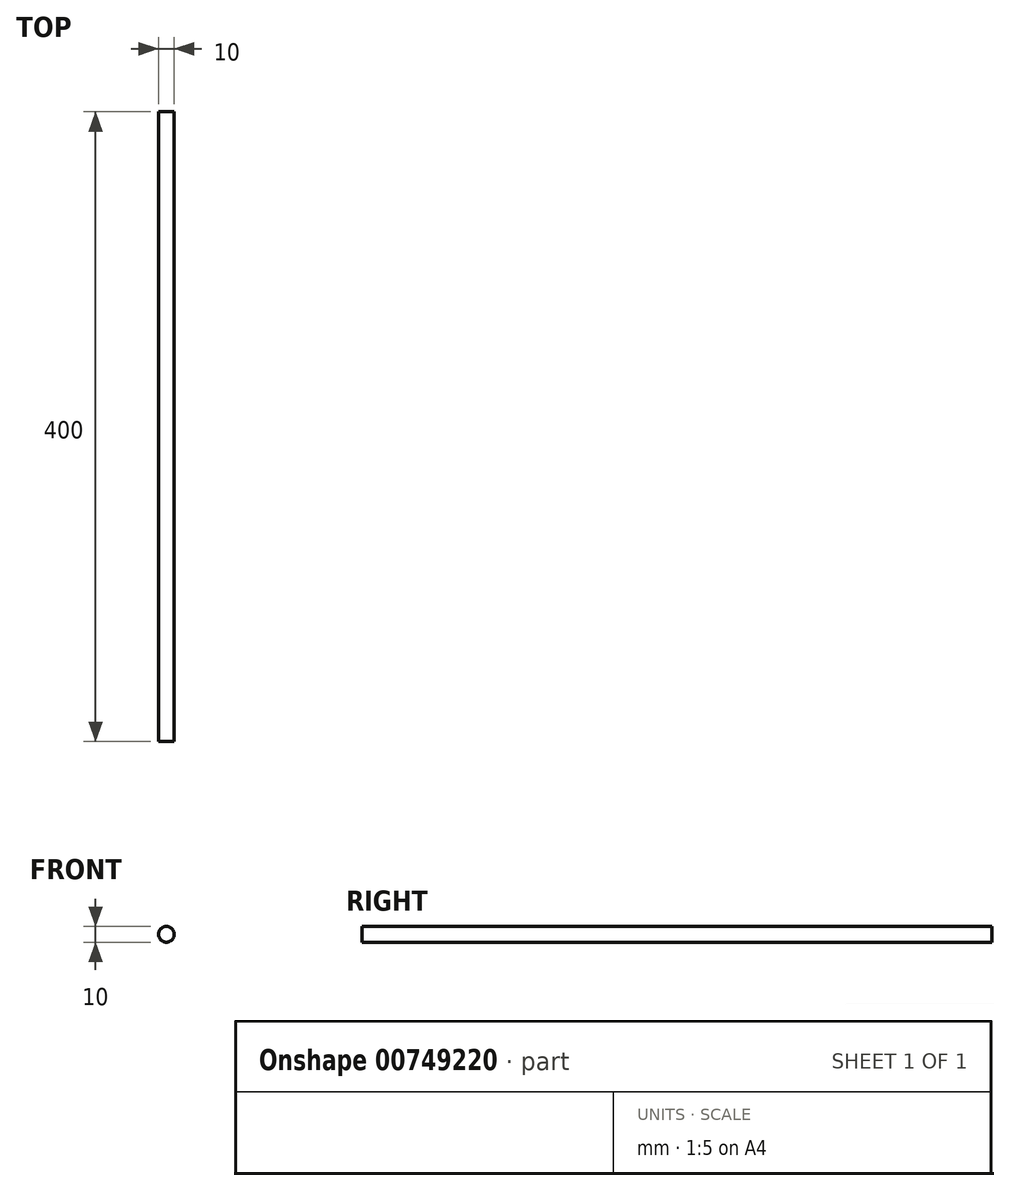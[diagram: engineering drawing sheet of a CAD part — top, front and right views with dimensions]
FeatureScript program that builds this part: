
annotation { "Feature Type Name" : "Feature", "Feature Type Description" : "" }
export const myFeature = defineFeature(function(context is Context, id is Id, definition is map)
    precondition{}
    {
        {
            var Q0;
            Q0=qCreatedBy(makeId("Front.planeOp"),FACE);
            var sketch = newSketch(context, id + "F0", { "sketchPlane" : qUnion([Q0])});
            skCircle(sketch, "E0", {"center": v(0, 0) * mm, "radius": 5 * mm});
            skSolve(sketch);
        }
        {
            var Q0;
            Q0=qSketchRegion(id+"F0",true);
            extrude(context, id + "F1", {"entities" : qUnion([Q0]), "depth" : 400 * mm, "offsetDistance" : 25 * mm});
        }
    });
